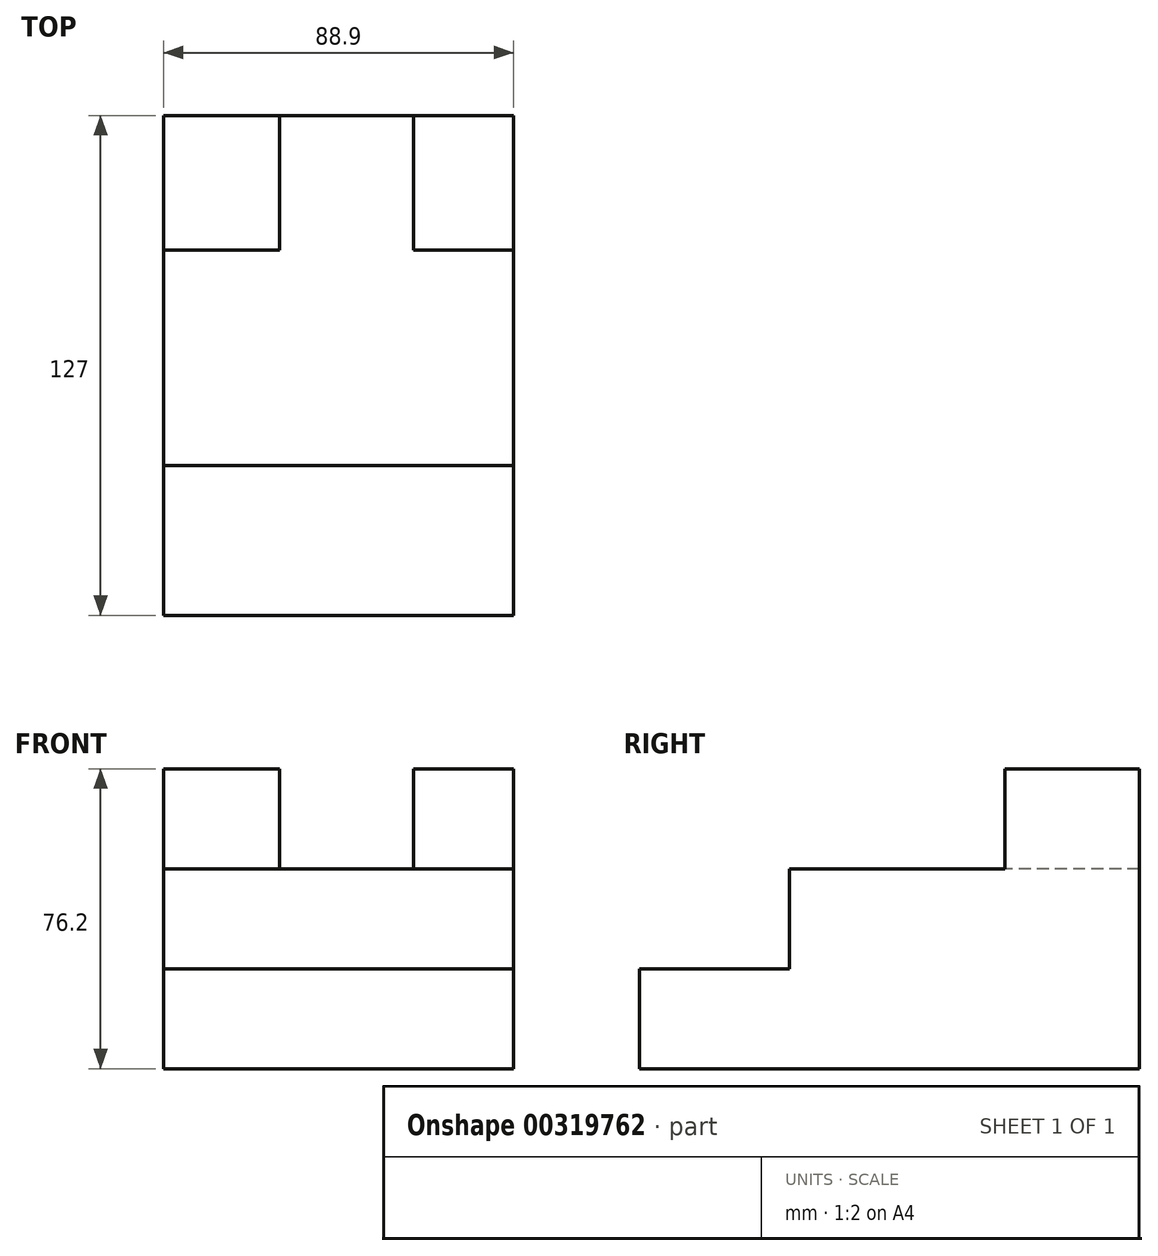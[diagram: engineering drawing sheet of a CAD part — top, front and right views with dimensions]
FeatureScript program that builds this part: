
annotation { "Feature Type Name" : "Feature", "Feature Type Description" : "" }
export const myFeature = defineFeature(function(context is Context, id is Id, definition is map)
    precondition{}
    {
        {
            var Q0;
            Q0=qCreatedBy(makeId("Right.planeOp"),FACE);
            var sketch = newSketch(context, id + "F0", { "sketchPlane" : qUnion([Q0])});
            skLineSegment(sketch, "E0", {"start": v(-54.7, 4.91) * mm, "end": v(34.2, 4.91) * mm});
            skLineSegment(sketch, "E1", {"start": v(34.2, 4.91) * mm, "end": v(34.2, -45.89) * mm});
            skLineSegment(sketch, "E2", {"start": v(34.2, -45.89) * mm, "end": v(-92.8, -45.89) * mm});
            skLineSegment(sketch, "E3", {"start": v(-92.8, -45.89) * mm, "end": v(-92.8, -20.49) * mm});
            skLineSegment(sketch, "E4", {"start": v(-92.8, -20.49) * mm, "end": v(-54.7, -20.49) * mm});
            skLineSegment(sketch, "E5", {"start": v(-54.7, -20.49) * mm, "end": v(-54.7, 4.91) * mm});
            skSolve(sketch);
        }
        {
            var Q0;
            Q0=makeQuery(id+"F0.imprint","IMPRINT",FACE,{"disambiguationData":[TD([[makeQuery(id+"F0.imprint","IMPRINT",EDGE,{"derivedFrom":sQuery(id+"F0.wireOp",EDGE,"E0")}),-1.0]])]});
            extrude(context, id + "F1", {"entities" : qUnion([Q0]), "depth" : 88.9 * mm});
        }
        {
            var Q0;
            Q0=makeQuery(id+"F1.opExtrude","SWEPT_FACE",FACE,{"disambiguationData":[OSD([sQuery(id+"F0.wireOp",EDGE,"E0")])]});
            var sketch = newSketch(context, id + "F2", { "sketchPlane" : qUnion([Q0])});
            skLineSegment(sketch, "E6.bottom", {"start": v(63.5, 34.2) * mm, "end": v(88.9, 34.2) * mm});
            skLineSegment(sketch, "E6.top", {"start": v(63.5, 0) * mm, "end": v(88.9, 0) * mm});
            skLineSegment(sketch, "E6.left", {"start": v(63.5, 34.2) * mm, "end": v(63.5, 0) * mm});
            skLineSegment(sketch, "E6.right", {"start": v(88.9, 34.2) * mm, "end": v(88.9, 0) * mm});
            skLineSegment(sketch, "E7.bottom", {"start": v(0, 34.2) * mm, "end": v(29.44, 34.2) * mm});
            skLineSegment(sketch, "E7.top", {"start": v(0, 0) * mm, "end": v(29.44, 0) * mm});
            skLineSegment(sketch, "E7.left", {"start": v(0, 34.2) * mm, "end": v(0, 0) * mm});
            skLineSegment(sketch, "E7.right", {"start": v(29.44, 34.2) * mm, "end": v(29.44, 0) * mm});
            skSolve(sketch);
        }
        {
            var Q0;
            Q0 = qSketchRegion(id + "F2", true);
            extrude(context, id + "F3", {"entities" : qUnion([Q0]), "operationType" : NewBodyOperationType.ADD, "depth" : 25.4 * mm});
        }
    });
